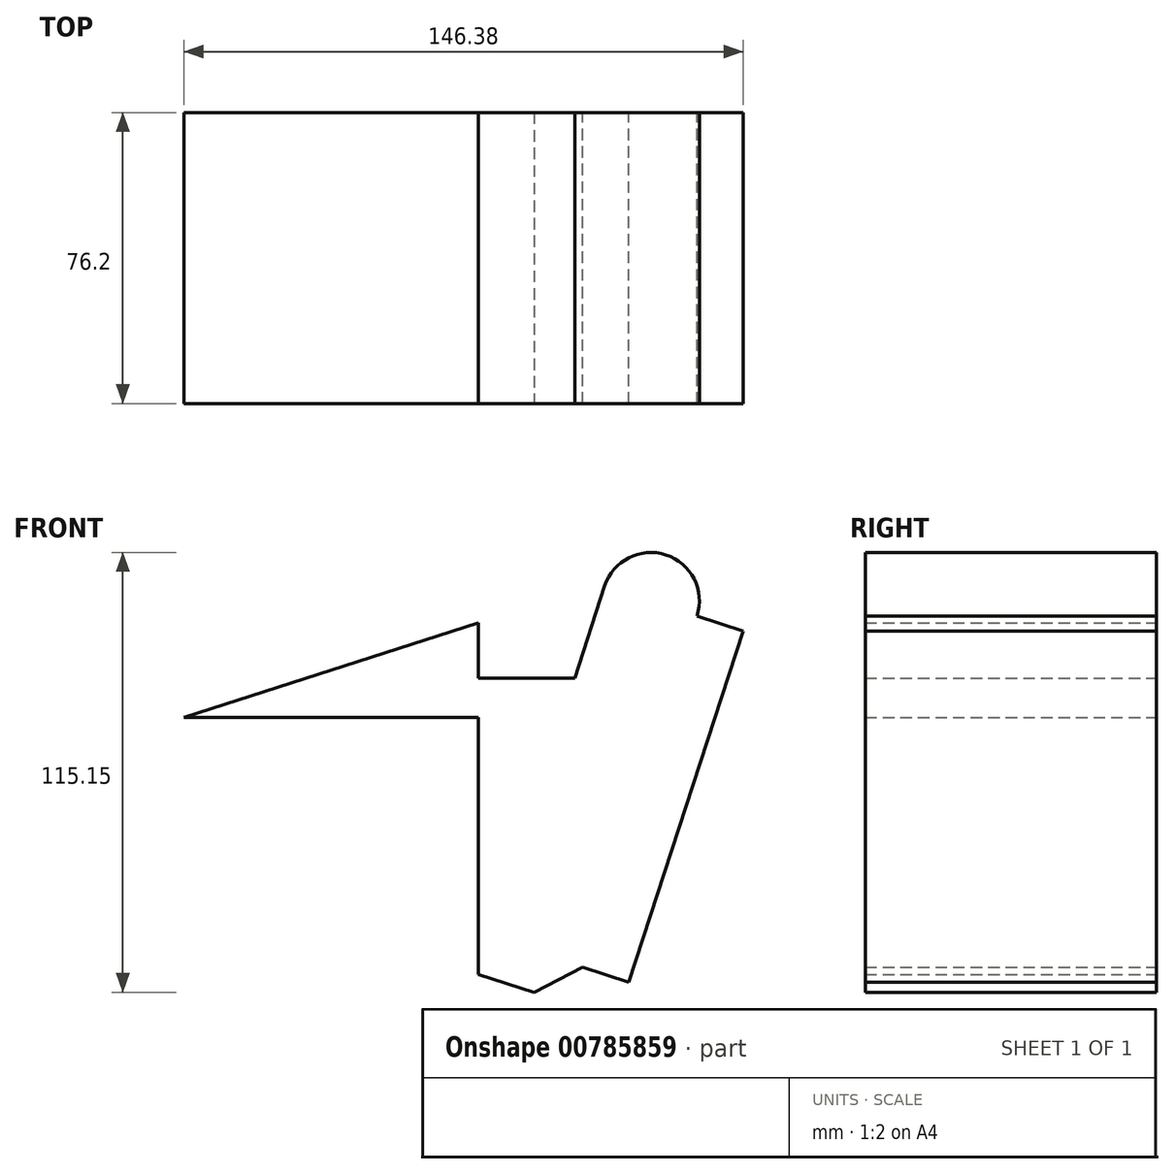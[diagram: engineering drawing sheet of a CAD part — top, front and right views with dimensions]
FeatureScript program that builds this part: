
annotation { "Feature Type Name" : "Feature", "Feature Type Description" : "" }
export const myFeature = defineFeature(function(context is Context, id is Id, definition is map)
    precondition{}
    {
        {
            var Q0;
            Q0=qCreatedBy(makeId("Front.planeOp"),FACE);
            var sketch = newSketch(context, id + "F0", { "sketchPlane" : qUnion([Q0])});
            skLineSegment(sketch, "E0.bottom", {"start": v(-34.03, 28.13) * mm, "end": v(43.08, 28.13) * mm});
            skLineSegment(sketch, "E0.top", {"start": v(-34.03, -39.15) * mm, "end": v(43.08, -39.15) * mm});
            skLineSegment(sketch, "E0.left", {"start": v(-34.03, 28.13) * mm, "end": v(-34.03, -39.15) * mm});
            skLineSegment(sketch, "E0.right", {"start": v(43.08, 28.13) * mm, "end": v(43.08, -39.15) * mm});
            skPoint(sketch, "E1.firstSnap0", {"position": v(43.08, -5.51) * mm});
            skLineSegment(sketch, "E1.bottom", {"start": v(43.08, 52.92) * mm, "end": v(68.26, 52.92) * mm});
            skLineSegment(sketch, "E1.top", {"start": v(43.08, 38.36) * mm, "end": v(68.26, 38.36) * mm});
            skLineSegment(sketch, "E1.left", {"start": v(43.08, 52.92) * mm, "end": v(43.08, 38.36) * mm});
            skLineSegment(sketch, "E1.right", {"start": v(68.26, 52.92) * mm, "end": v(68.26, 38.36) * mm});
            skLineSegment(sketch, "E2", {"start": v(-34.03, 28.13) * mm, "end": v(43.08, 52.92) * mm});
            skLineSegment(sketch, "E3", {"start": v(43.08, -39.15) * mm, "end": v(68.26, 38.36) * mm});
            skSolve(sketch);
        }
        {
            var Q0;
            Q0=makeQuery(id+"F0.imprint","IMPRINT",FACE,{"disambiguationData":[TD([[makeQuery(id+"F0.imprint","IMPRINT",EDGE,{"derivedFrom":sQuery(id+"F0.wireOp",EDGE,"E0.bottom")}),1.0]])]});
            extrude(context, id + "F1", {"entities" : qUnion([Q0]), "endBound" : BoundingType.SYMMETRIC, "depth" : 76.2 * mm, "offsetDistance" : 25.4 * mm});
        }
        {
            var Q0;
            Q0=makeQuery(id+"F1.opExtrude","SWEPT_FACE",FACE,{"disambiguationData":[OSD([sQuery(id+"F0.wireOp",EDGE,"E3")])]});
            var Q1;
            Q1=makeQuery(id+"F1.opExtrude","SWEPT_FACE",FACE,{"disambiguationData":[OSD([sQuery(id+"F0.wireOp",EDGE,"E1.top")])]});
            extrude(context, id + "F2", {"entities" : qUnion([Q0, Q1]), "operationType" : NewBodyOperationType.ADD, "depth" : 25.4 * mm, "offsetDistance" : 25.4 * mm});
        }
        {
            var Q0;
            Q0=makeQuery(id+"F2.opExtrude","SWEPT_FACE",FACE,{"disambiguationData":[OSD([sQuery(id+"F0.wireOp",EDGE,"E1.top"),sQuery(id+"F0.wireOp",EDGE,"E1.right"),sQuery(id+"F0.wireOp",EDGE,"E3")]),OD(1.0)]});
            extrude(context, id + "F3", {"entities" : qUnion([Q0]), "operationType" : NewBodyOperationType.ADD, "depth" : 38.1 * mm, "offsetDistance" : 25.4 * mm});
        }
        {
            var Q0;
            {var subQ0=sQuery(id+"F0.wireOp",EDGE,"E3");var subQ1=sQuery(id+"F0.wireOp",EDGE,"E1.right");var subQ2=sQuery(id+"F0.wireOp",EDGE,"E1.top");Q0=makeQuery(id+"F3.opExtrude","CAP_EDGE",EDGE,{"disambiguationData":[OSD([subQ2,subQ1,subQ0]),TDD([makeQuery(id+"F2.boolean.opBoolean","MERGE",EDGE,{"derivedFrom":[makeQuery(id+"F2.opExtrude","CAP_EDGE",EDGE,{"disambiguationData":[OSD([subQ2,subQ1,subQ0]),OD(0.0)],"isStart":false}),makeQuery(id+"F2.opExtrude","CAP_EDGE",EDGE,{"disambiguationData":[OSD([subQ2,subQ1,subQ0]),OD(2.0)],"isStart":false})]})])],"isStart":false});}
            var Q1;
            {var subQ0=sQuery(id+"F0.wireOp",EDGE,"E3");var subQ1=sQuery(id+"F0.wireOp",EDGE,"E1.right");var subQ2=sQuery(id+"F0.wireOp",EDGE,"E1.top");Q1=makeQuery(id+"F3.opExtrude","CAP_EDGE",EDGE,{"disambiguationData":[OSD([subQ2,subQ1,subQ0]),TDD([makeQuery(id+"F2.boolean.opBoolean","MERGE",EDGE,{"derivedFrom":[makeQuery(id+"F1.opExtrude","SWEPT_EDGE",EDGE,{"disambiguationData":[OSD([subQ2,subQ1,subQ0])]}),makeQuery(id+"F2.opExtrude","CAP_EDGE",EDGE,{"disambiguationData":[OSD([subQ2,subQ1,subQ0]),OD(1.0)],"isStart":false})]})])],"isStart":false});}
            fillet(context, id + "F4", {"entities" : qUnion([Q0, Q1]), "radius" : 12.7 * mm, "tangentPropagation" : true, "allowEdgeOverflow" : false});
        }
        {
            var Q0;
            Q0=makeQuery(id+"F2.opExtrude","CAP_EDGE",EDGE,{"disambiguationData":[OSD([sQuery(id+"F0.wireOp",EDGE,"E0.top"),sQuery(id+"F0.wireOp",EDGE,"E0.right"),sQuery(id+"F0.wireOp",EDGE,"E3")])],"isStart":false});
            chamfer(context, id + "F5", {"entities" : qUnion([Q0]), "width" : 10.16 * mm, "tangentPropagation" : true});
        }
        {
            var Q0;
            {var subQ0=sQuery(id+"F0.wireOp",EDGE,"E3");var subQ1=sQuery(id+"F0.wireOp",EDGE,"E1.right");var subQ2=sQuery(id+"F0.wireOp",EDGE,"E1.top");Q0=makeQuery(id+"F3.boolean.opBoolean","MERGE",FACE,{"derivedFrom":[makeQuery(id+"F2.opExtrude","CAP_FACE",FACE,{"disambiguationData":[OSD([subQ0])],"isStart":false}),makeQuery(id+"F3.opExtrude","SWEPT_FACE",FACE,{"disambiguationData":[OSD([subQ2,subQ1,subQ0]),TDD([makeQuery(id+"F2.boolean.opBoolean","MERGE",EDGE,{"derivedFrom":[makeQuery(id+"F2.opExtrude","CAP_EDGE",EDGE,{"disambiguationData":[OSD([subQ2,subQ1,subQ0]),OD(0.0)],"isStart":false}),makeQuery(id+"F2.opExtrude","CAP_EDGE",EDGE,{"disambiguationData":[OSD([subQ2,subQ1,subQ0]),OD(2.0)],"isStart":false})]})])]})]});}
            extrude(context, id + "F6", {"entities" : qUnion([Q0]), "operationType" : NewBodyOperationType.ADD, "depth" : 12.7 * mm, "offsetDistance" : 25.4 * mm});
        }
    });
